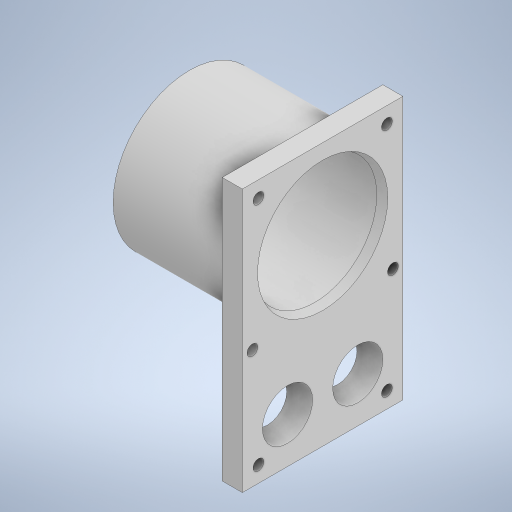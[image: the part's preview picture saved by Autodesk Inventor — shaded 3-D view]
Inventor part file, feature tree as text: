
AUTODESK INVENTOR PART (.ipt)
format: ipt  version: 2023 (Build 270158000, 158)  size: 299,008 bytes
history: native  units: in
note: dims shown in document units (in); Inventor stores cm internally (conversion verified against a paired STEP export)
features: extrude x2, chamfer x2, draft x1
ambient origin geometry x8: Origin, YZ Plane, XZ Plane, XY Plane, X Axis, Y Axis, Z Axis, Center Point
bodies: Solid1 (feature_tree)
feature tree (5):
  extrude  "Extrusion1"  Depth=3.275in
  draft  "FaceDraft1"
  extrude  "Extrusion2"  Depth=2.0in
  chamfer  "Chamfer1"  Distance=1.55in
  chamfer  "Chamfer2"  Distance=1.0in
